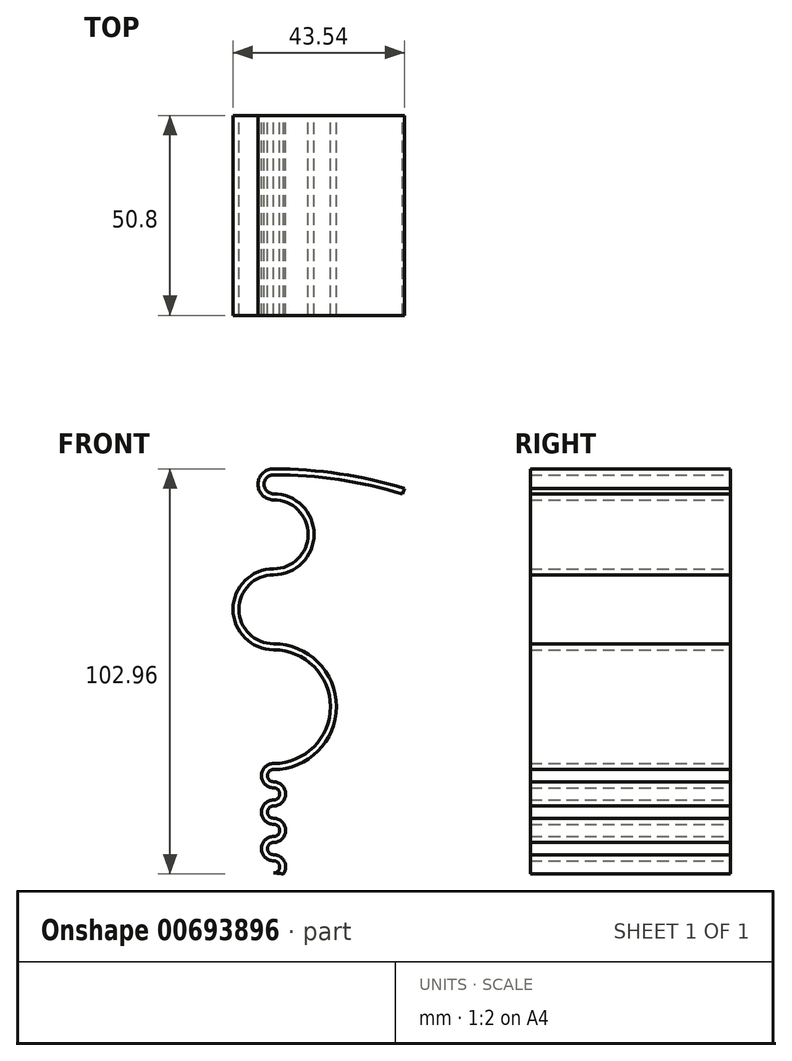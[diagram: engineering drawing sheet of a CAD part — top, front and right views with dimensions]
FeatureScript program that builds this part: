
annotation { "Feature Type Name" : "Feature", "Feature Type Description" : "" }
export const myFeature = defineFeature(function(context is Context, id is Id, definition is map)
    precondition{}
    {
        {
            var Q0;
            Q0=qCreatedBy(makeId("Front.planeOp"),FACE);
            var sketch = newSketch(context, id + "F0", { "sketchPlane" : qUnion([Q0])});
            skArc(sketch, "E0", {"start": v(0, 38.1) * mm, "mid": v(15.21, 53.31) * mm, "end": v(0, 68.52) * mm, "construction": true});
            skArc(sketch, "E1", {"start": v(0, 68.52) * mm, "mid": v(-9.53, 78.05) * mm, "end": v(0, 87.57) * mm, "construction": true});
            skArc(sketch, "E2", {"start": v(0, 87.57) * mm, "mid": v(9.52, 97.1) * mm, "end": v(0, 106.62) * mm, "construction": true});
            skArc(sketch, "E3", {"start": v(0, 106.62) * mm, "mid": v(-3.18, 109.8) * mm, "end": v(0, 112.97) * mm, "construction": true});
            skLineSegment(sketch, "E4", {"start": v(0, 38.1) * mm, "end": v(0, 38.1) * mm});
            skArc(sketch, "E5", {"start": v(0, 38.1) * mm, "mid": v(-2.32, 35.78) * mm, "end": v(0, 33.46) * mm, "construction": true});
            skLineSegment(sketch, "E6", {"start": v(0, 33.46) * mm, "end": v(0, 33.46) * mm});
            skArc(sketch, "E7", {"start": v(0, 33.46) * mm, "mid": v(2.32, 31.15) * mm, "end": v(0, 28.83) * mm, "construction": true});
            skLineSegment(sketch, "E8", {"start": v(0, 38.1) * mm, "end": v(0, 16.93) * mm, "construction": true});
            skArc(sketch, "E9.1.0.0", {"start": v(0, 24.2) * mm, "mid": v(2.32, 21.88) * mm, "end": v(0, 19.56) * mm, "construction": true});
            skLineSegment(sketch, "E9.1.0.1", {"start": v(0, 24.2) * mm, "end": v(0, 24.2) * mm});
            skLineSegment(sketch, "E9.1.0.2", {"start": v(0, 28.83) * mm, "end": v(0, 28.83) * mm});
            skArc(sketch, "E9.1.0.3", {"start": v(0, 28.83) * mm, "mid": v(-2.32, 26.51) * mm, "end": v(0, 24.2) * mm, "construction": true});
            skArc(sketch, "E9.2.0.0", {"start": v(0, 14.92) * mm, "mid": v(2.15, 13.47) * mm, "end": v(1.6, 10.93) * mm, "construction": true});
            skLineSegment(sketch, "E9.2.0.1", {"start": v(0, 14.92) * mm, "end": v(0, 14.92) * mm});
            skLineSegment(sketch, "E9.2.0.2", {"start": v(0, 19.56) * mm, "end": v(0, 19.56) * mm});
            skArc(sketch, "E9.2.0.3", {"start": v(0, 19.56) * mm, "mid": v(-2.32, 17.24) * mm, "end": v(0, 14.92) * mm, "construction": true});
            skLineSegment(sketch, "E9.direction1", {"start": v(0, 38.1) * mm, "end": v(0, 28.83) * mm, "construction": true});
            skArc(sketch, "E10.0", {"start": v(0, 14.16) * mm, "mid": v(1.56, 12.6) * mm, "end": v(0, 11.05) * mm});
            skLineSegment(sketch, "E10.1", {"start": v(0, 14.16) * mm, "end": v(0, 14.16) * mm});
            skArc(sketch, "E10.2", {"start": v(0, 20.32) * mm, "mid": v(-3.08, 17.24) * mm, "end": v(0, 14.16) * mm});
            skLineSegment(sketch, "E10.3", {"start": v(0, 20.32) * mm, "end": v(0, 20.32) * mm});
            skArc(sketch, "E10.4", {"start": v(0, 23.43) * mm, "mid": v(1.56, 21.88) * mm, "end": v(0, 20.32) * mm});
            skLineSegment(sketch, "E10.5", {"start": v(0, 23.43) * mm, "end": v(0, 23.43) * mm});
            skArc(sketch, "E10.6", {"start": v(0, 29.6) * mm, "mid": v(-3.08, 26.51) * mm, "end": v(0, 23.43) * mm});
            skArc(sketch, "E10.7", {"start": v(0, 67.76) * mm, "mid": v(-10.29, 78.05) * mm, "end": v(0, 88.33) * mm});
            skArc(sketch, "E10.8", {"start": v(0, 88.33) * mm, "mid": v(8.76, 97.1) * mm, "end": v(0, 105.86) * mm});
            skArc(sketch, "E10.9", {"start": v(0, 105.86) * mm, "mid": v(-3.94, 109.8) * mm, "end": v(0, 113.73) * mm});
            skArc(sketch, "E10.11", {"start": v(0, 38.86) * mm, "mid": v(14.45, 53.31) * mm, "end": v(0, 67.76) * mm});
            skLineSegment(sketch, "E10.12", {"start": v(0, 38.86) * mm, "end": v(0, 38.86) * mm});
            skArc(sketch, "E10.13", {"start": v(0, 38.86) * mm, "mid": v(-3.08, 35.78) * mm, "end": v(0, 32.7) * mm});
            skLineSegment(sketch, "E10.14", {"start": v(0, 32.7) * mm, "end": v(0, 32.7) * mm});
            skArc(sketch, "E10.15", {"start": v(0, 32.7) * mm, "mid": v(1.56, 31.15) * mm, "end": v(0, 29.6) * mm});
            skLineSegment(sketch, "E10.16", {"start": v(0, 29.6) * mm, "end": v(0, 29.6) * mm});
            skArc(sketch, "E11.0", {"start": v(0, 15.68) * mm, "mid": v(2.75, 13.99) * mm, "end": v(2.47, 10.77) * mm});
            skLineSegment(sketch, "E11.1", {"start": v(0, 15.68) * mm, "end": v(0, 15.68) * mm});
            skArc(sketch, "E11.2", {"start": v(0, 18.8) * mm, "mid": v(-1.56, 17.24) * mm, "end": v(0, 15.68) * mm});
            skLineSegment(sketch, "E11.3", {"start": v(0, 18.8) * mm, "end": v(0, 18.8) * mm});
            skArc(sketch, "E11.4", {"start": v(0, 24.96) * mm, "mid": v(3.08, 21.88) * mm, "end": v(0, 18.8) * mm});
            skLineSegment(sketch, "E11.5", {"start": v(0, 24.96) * mm, "end": v(0, 24.96) * mm});
            skArc(sketch, "E11.6", {"start": v(0, 28.07) * mm, "mid": v(-1.56, 26.51) * mm, "end": v(0, 24.96) * mm});
            skArc(sketch, "E11.7", {"start": v(0, 69.28) * mm, "mid": v(-8.76, 78.05) * mm, "end": v(0, 86.8) * mm});
            skArc(sketch, "E11.8", {"start": v(0, 86.8) * mm, "mid": v(10.29, 97.1) * mm, "end": v(0, 107.38) * mm});
            skArc(sketch, "E11.9", {"start": v(0, 107.38) * mm, "mid": v(-2.41, 109.8) * mm, "end": v(0, 112.2) * mm});
            skArc(sketch, "E11.11", {"start": v(0, 37.34) * mm, "mid": v(15.97, 53.31) * mm, "end": v(0, 69.28) * mm});
            skLineSegment(sketch, "E11.12", {"start": v(0, 37.34) * mm, "end": v(0, 37.34) * mm});
            skArc(sketch, "E11.13", {"start": v(0, 37.34) * mm, "mid": v(-1.56, 35.78) * mm, "end": v(0, 34.23) * mm});
            skLineSegment(sketch, "E11.14", {"start": v(0, 34.23) * mm, "end": v(0, 34.23) * mm});
            skArc(sketch, "E11.15", {"start": v(0, 34.23) * mm, "mid": v(3.08, 31.15) * mm, "end": v(0, 28.07) * mm});
            skLineSegment(sketch, "E11.16", {"start": v(0, 28.07) * mm, "end": v(0, 28.07) * mm});
            skArc(sketch, "E12", {"start": v(2.47, 10.77) * mm, "mid": v(1.24, 10.98) * mm, "end": v(0, 11.05) * mm});
            skPoint(sketch, "E13.orphan", {"position": v(0, 10.29) * mm});
            skArc(sketch, "E14", {"start": v(0, 112.97) * mm, "mid": v(16.7, 111.73) * mm, "end": v(33.03, 108.03) * mm, "construction": true});
            skArc(sketch, "E15.0", {"start": v(0, 112.2) * mm, "mid": v(16.59, 110.98) * mm, "end": v(32.8, 107.3) * mm});
            skArc(sketch, "E16.0", {"start": v(0, 113.73) * mm, "mid": v(16.81, 112.48) * mm, "end": v(33.25, 108.76) * mm});
            skLineSegment(sketch, "E17", {"start": v(33.25, 108.76) * mm, "end": v(32.8, 107.3) * mm});
            skLineSegment(sketch, "E18", {"start": v(0, 0) * mm, "end": v(0, 112.97) * mm, "construction": true});
            skLineSegment(sketch, "E19", {"start": v(33.03, 108.03) * mm, "end": v(0, 0) * mm, "construction": true});
            skSolve(sketch);
        }
        {
            var Q0;
            Q0 = qSketchRegion(id + "F0", true);
            var Q1;
            Q1 = qConstructionFilter(qBodyType(qCreatedBy(id + "F0" ,EDGE), BodyType.WIRE), ConstructionObject.NO);
            extrude(context, id + "F1", {"entities" : qUnion([Q0]), "surfaceEntities" : qUnion([Q1]), "depth" : 50.8 * mm, "offsetDistance" : 25.4 * mm});
        }
        {
            var Q0;
            Q0=qCreatedBy(makeId("Top.planeOp"),FACE);
            var sketch = newSketch(context, id + "F2", { "sketchPlane" : qUnion([Q0])});
            skLineSegment(sketch, "E20", {"start": v(0, 0) * mm, "end": v(0, 48.67) * mm, "construction": true});
            skSolve(sketch);
        }
    });
